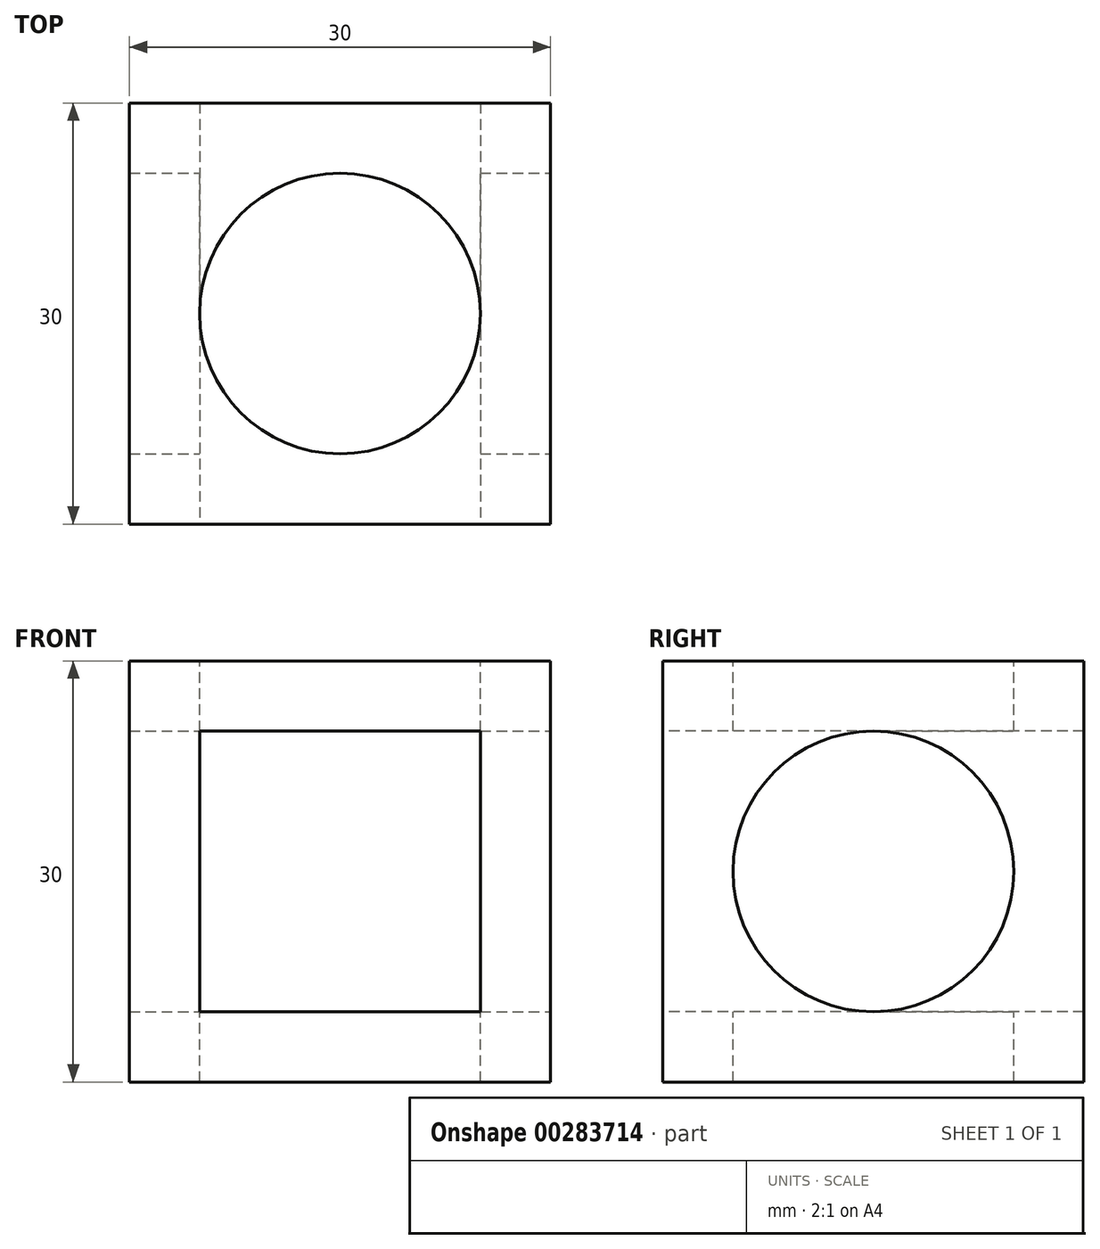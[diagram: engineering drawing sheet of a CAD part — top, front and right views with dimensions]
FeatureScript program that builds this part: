
annotation { "Feature Type Name" : "Feature", "Feature Type Description" : "" }
export const myFeature = defineFeature(function(context is Context, id is Id, definition is map)
    precondition{}
    {
        {
            var Q0;
            Q0=qCreatedBy(makeId("Front.planeOp"),FACE);
            var sketch = newSketch(context, id + "F0", { "sketchPlane" : qUnion([Q0])});
            skLineSegment(sketch, "E0.bottom", {"start": v(15, 15) * mm, "end": v(-15, 15) * mm});
            skLineSegment(sketch, "E0.top", {"start": v(15, -15) * mm, "end": v(-15, -15) * mm});
            skLineSegment(sketch, "E0.left", {"start": v(15, 15) * mm, "end": v(15, -15) * mm});
            skLineSegment(sketch, "E0.right", {"start": v(-15, 15) * mm, "end": v(-15, -15) * mm});
            skPoint(sketch, "E0.middle", {"position": v(0, 0) * mm});
            skSolve(sketch);
        }
        {
            var Q0;
            Q0 = qSketchRegion(id + "F0", true);
            extrude(context, id + "F1", {"entities" : qUnion([Q0]), "endBound" : BoundingType.SYMMETRIC, "depth" : 30 * mm});
        }
        {
            var Q0;
            Q0=makeQuery(id+"F1.opExtrude","CAP_FACE",FACE,{"disambiguationData":[OSD([sQuery(id+"F0.wireOp",EDGE,"E0.bottom"),sQuery(id+"F0.wireOp",EDGE,"E0.top"),sQuery(id+"F0.wireOp",EDGE,"E0.left"),sQuery(id+"F0.wireOp",EDGE,"E0.right")])],"isStart":false});
            var sketch = newSketch(context, id + "F2", { "sketchPlane" : qUnion([Q0])});
            skLineSegment(sketch, "E1.bottom", {"start": v(10, 10) * mm, "end": v(-10, 10) * mm});
            skLineSegment(sketch, "E1.top", {"start": v(10, -10) * mm, "end": v(-10, -10) * mm});
            skLineSegment(sketch, "E1.left", {"start": v(10, 10) * mm, "end": v(10, -10) * mm});
            skLineSegment(sketch, "E1.right", {"start": v(-10, 10) * mm, "end": v(-10, -10) * mm});
            skPoint(sketch, "E1.middle", {"position": v(0, 0) * mm});
            skSolve(sketch);
        }
        {
            var Q0;
            Q0 = qSketchRegion(id + "F2", true);
            extrude(context, id + "F3", {"entities" : qUnion([Q0]), "operationType" : NewBodyOperationType.REMOVE, "endBound" : BoundingType.THROUGH_ALL, "oppositeDirection" : true, "depth" : 25 * mm});
        }
        {
            var Q0;
            Q0=makeQuery(id+"F1.opExtrude","SWEPT_FACE",FACE,{"disambiguationData":[OSD([sQuery(id+"F0.wireOp",EDGE,"E0.left")])]});
            var sketch = newSketch(context, id + "F4", { "sketchPlane" : qUnion([Q0])});
            skCircle(sketch, "E2", {"center": v(0, 0) * mm, "radius": 10 * mm});
            skPoint(sketch, "E2.centerSnap0", {"position": v(0, -15) * mm});
            skSolve(sketch);
        }
        {
            var Q0;
            Q0 = qSketchRegion(id + "F4", true);
            extrude(context, id + "F5", {"entities" : qUnion([Q0]), "operationType" : NewBodyOperationType.REMOVE, "endBound" : BoundingType.THROUGH_ALL, "oppositeDirection" : true, "depth" : 25 * mm});
        }
        {
            var Q0;
            Q0=makeQuery(id+"F1.opExtrude","SWEPT_FACE",FACE,{"disambiguationData":[OSD([sQuery(id+"F0.wireOp",EDGE,"E0.bottom")])]});
            var sketch = newSketch(context, id + "F6", { "sketchPlane" : qUnion([Q0])});
            skCircle(sketch, "E3", {"center": v(0, 0) * mm, "radius": 10 * mm});
            skSolve(sketch);
        }
        {
            var Q0;
            Q0=makeQuery(id+"F6.imprint","IMPRINT",FACE,{"disambiguationData":[TD([[makeQuery(id+"F6.imprint","IMPRINT",EDGE,{"derivedFrom":sQuery(id+"F6.wireOp",EDGE,"E3")}),1.0]])]});
            extrude(context, id + "F7", {"entities" : qUnion([Q0]), "operationType" : NewBodyOperationType.REMOVE, "endBound" : BoundingType.THROUGH_ALL, "oppositeDirection" : true, "depth" : 25 * mm});
        }
    });
